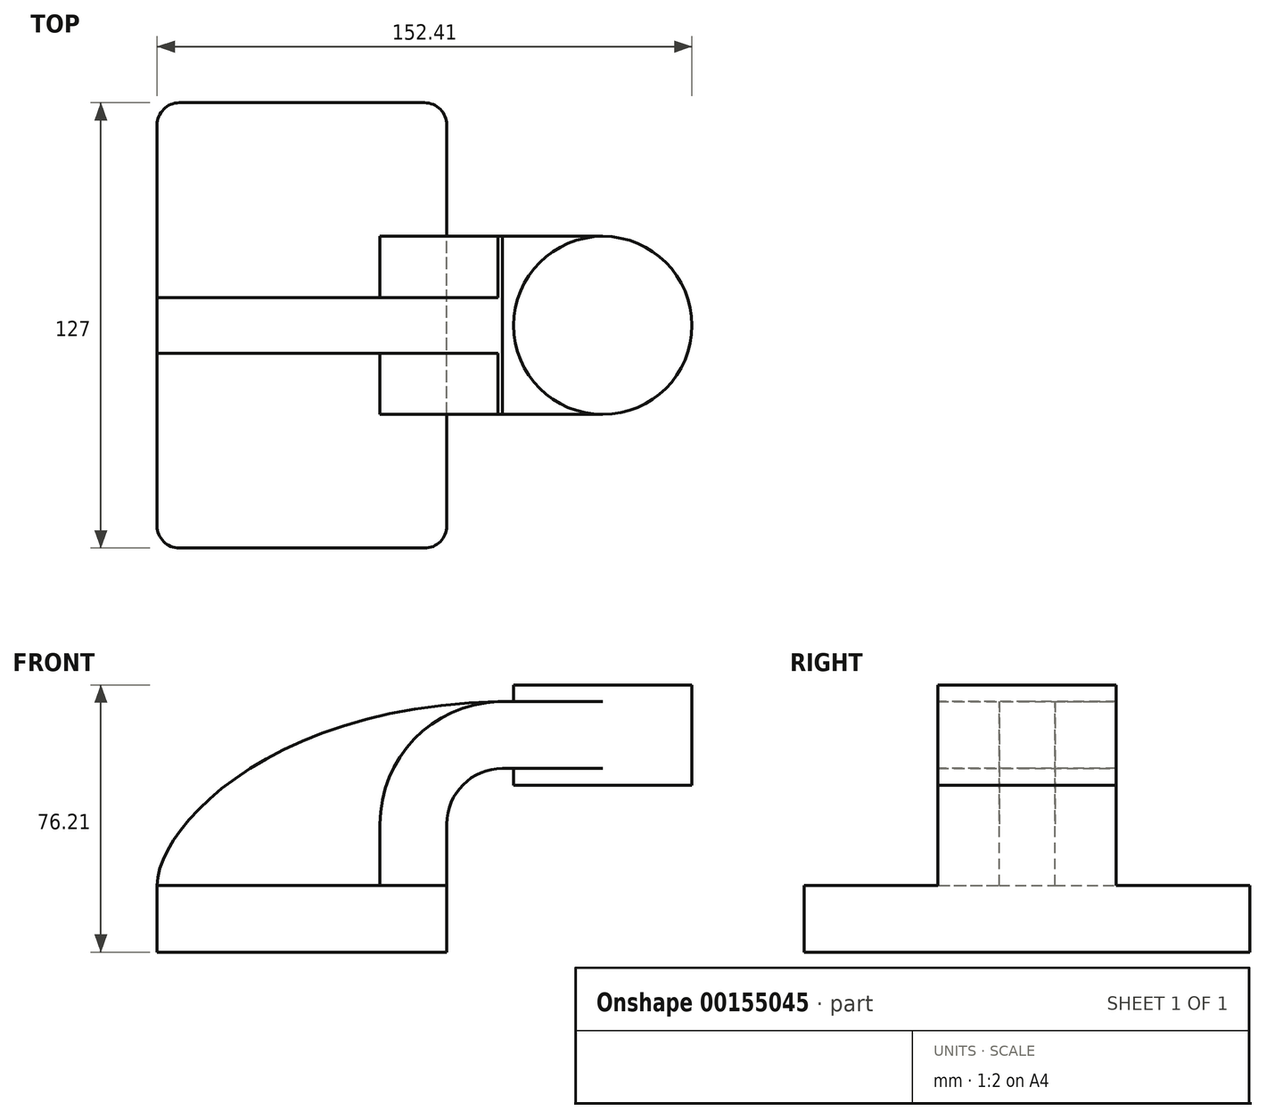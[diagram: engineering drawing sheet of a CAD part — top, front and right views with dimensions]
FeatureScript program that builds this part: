
annotation { "Feature Type Name" : "Feature", "Feature Type Description" : "" }
export const myFeature = defineFeature(function(context is Context, id is Id, definition is map)
    precondition{}
    {
        {
            var Q0;
            Q0=qCreatedBy(makeId("Front.planeOp"),FACE);
            var sketch = newSketch(context, id + "F0", { "sketchPlane" : qUnion([Q0])});
            skLineSegment(sketch, "E0.bottom", {"start": v(41.27, 9.53) * mm, "end": v(-41.28, 9.53) * mm});
            skLineSegment(sketch, "E0.top", {"start": v(41.28, -9.52) * mm, "end": v(-41.27, -9.52) * mm});
            skLineSegment(sketch, "E0.left", {"start": v(41.28, 9.53) * mm, "end": v(41.28, -9.52) * mm});
            skLineSegment(sketch, "E0.right", {"start": v(-41.28, 9.53) * mm, "end": v(-41.27, -9.52) * mm});
            skPoint(sketch, "E0.middle", {"position": v(0, 0) * mm});
            skLineSegment(sketch, "E1.bottom", {"start": v(111.12, 66.68) * mm, "end": v(60.32, 66.68) * mm});
            skLineSegment(sketch, "E1.top", {"start": v(111.13, 38.1) * mm, "end": v(60.32, 38.1) * mm});
            skLineSegment(sketch, "E1.left", {"start": v(111.12, 66.68) * mm, "end": v(111.13, 38.1) * mm});
            skLineSegment(sketch, "E1.right", {"start": v(60.32, 66.68) * mm, "end": v(60.32, 38.1) * mm});
            skPoint(sketch, "E1.middle", {"position": v(85.72, 52.39) * mm});
            skLineSegment(sketch, "E2", {"start": v(41.27, 9.53) * mm, "end": v(41.27, 26.99) * mm});
            skArc(sketch, "E3", {"start": v(41.27, 26.99) * mm, "mid": v(45.92, 38.21) * mm, "end": v(57.15, 42.86) * mm});
            skLineSegment(sketch, "E4", {"start": v(57.15, 42.86) * mm, "end": v(85.72, 42.86) * mm});
            skLineSegment(sketch, "E5.0", {"start": v(57.15, 61.91) * mm, "end": v(85.72, 61.91) * mm});
            skArc(sketch, "E5.1", {"start": v(22.23, 26.99) * mm, "mid": v(32.45, 51.68) * mm, "end": v(57.15, 61.91) * mm});
            skLineSegment(sketch, "E5.2", {"start": v(22.22, 9.53) * mm, "end": v(22.22, 26.99) * mm});
            skLineSegment(sketch, "E6", {"start": v(85.72, 38.1) * mm, "end": v(85.72, 66.68) * mm});
            skFitSpline(sketch, "E7", {"points": [v(-41.28, 9.53) * mm, v(57.15, 61.91) * mm], "startDerivative": vector(0.8, 50.37) * mm, "endDerivative": vector(197.18, 2.96) * mm});
            skSolve(sketch);
        }
        {
            var Q0;
            Q0=makeQuery(id+"F0.imprint","IMPRINT",FACE,{"disambiguationData":[TD([[makeQuery(id+"F0.imprint","IMPRINT",EDGE,{"derivedFrom":sQuery(id+"F0.wireOp",EDGE,"E0.top")}),-1.0]])]});
            extrude(context, id + "F1", {"entities" : qUnion([Q0]), "endBound" : BoundingType.SYMMETRIC, "depth" : 127 * mm});
        }
        {
            var Q0;
            {var subQ1=sQuery(id+"F0.wireOp",EDGE,"E2");Q0=makeQuery(id+"F0.imprint","IMPRINT",FACE,{"disambiguationData":[TD([[makeQuery(id+"F0.imprint","IMPRINT",EDGE,{"derivedFrom":subQ1}),1.0]])]});}
            var Q1;
            {var subQ0=sQuery(id+"F0.wireOp",EDGE,"E5.0");var subQ1=sQuery(id+"F0.wireOp",EDGE,"E1.right");var subQ2=makeQuery(id+"F0.imprint","INTERSECT",VERTEX,{"derivedFrom":[subQ1,subQ0]});Q1=makeQuery(id+"F0.imprint","IMPRINT",FACE,{"disambiguationData":[TD([[makeQuery(id+"F0.imprint","IMPRINT",EDGE,{"disambiguationData":[TD([[subQ2,-1.0]])],"derivedFrom":subQ1}),1.0]])]});}
            extrude(context, id + "F2", {"entities" : qUnion([Q0, Q1]), "operationType" : NewBodyOperationType.ADD, "endBound" : BoundingType.SYMMETRIC, "depth" : 50.8 * mm});
        }
        {
            var Q0;
            {var subQ3=sQuery(id+"F0.wireOp",EDGE,"E5.2");Q0=makeQuery(id+"F0.imprint","IMPRINT",FACE,{"disambiguationData":[TD([[makeQuery(id+"F0.imprint","IMPRINT",EDGE,{"derivedFrom":subQ3}),1.0]])]});}
            extrude(context, id + "F3", {"entities" : qUnion([Q0]), "operationType" : NewBodyOperationType.ADD, "endBound" : BoundingType.SYMMETRIC, "depth" : 15.88 * mm});
        }
        {
            var Q0;
            {var subQ0=sQuery(id+"F0.wireOp",EDGE,"E1.left");Q0=makeQuery(id+"F0.imprint","IMPRINT",FACE,{"disambiguationData":[TD([[makeQuery(id+"F0.imprint","IMPRINT",EDGE,{"derivedFrom":subQ0}),-1.0]])]});}
            var Q1;
            Q1=sQuery(id+"F0.wireOp",EDGE,"E6");
            revolve(context, id + "F4", {"operationType" : NewBodyOperationType.ADD, "entities" : qUnion([Q0]), "axis" : qUnion([Q1]), "revolveType" : RevolveType.FULL});
        }
        {
            var Q0;
            Q0=makeQuery(id+"F1.opExtrude","CAP_EDGE",EDGE,{"disambiguationData":[OSD([sQuery(id+"F0.wireOp",EDGE,"E0.left")])],"isStart":false});
            var Q1;
            Q1=makeQuery(id+"F1.opExtrude","CAP_EDGE",EDGE,{"disambiguationData":[OSD([sQuery(id+"F0.wireOp",EDGE,"E0.left")])],"isStart":true});
            var Q2;
            Q2=makeQuery(id+"F1.opExtrude","CAP_EDGE",EDGE,{"disambiguationData":[OSD([sQuery(id+"F0.wireOp",EDGE,"E0.right")])],"isStart":false});
            var Q3;
            Q3=makeQuery(id+"F1.opExtrude","CAP_EDGE",EDGE,{"disambiguationData":[OSD([sQuery(id+"F0.wireOp",EDGE,"E0.right")])],"isStart":true});
            fillet(context, id + "F5", {"entities" : qUnion([Q0, Q1, Q2, Q3]), "radius" : 6.35 * mm, "tangentPropagation" : true, "allowEdgeOverflow" : false});
        }
    });
